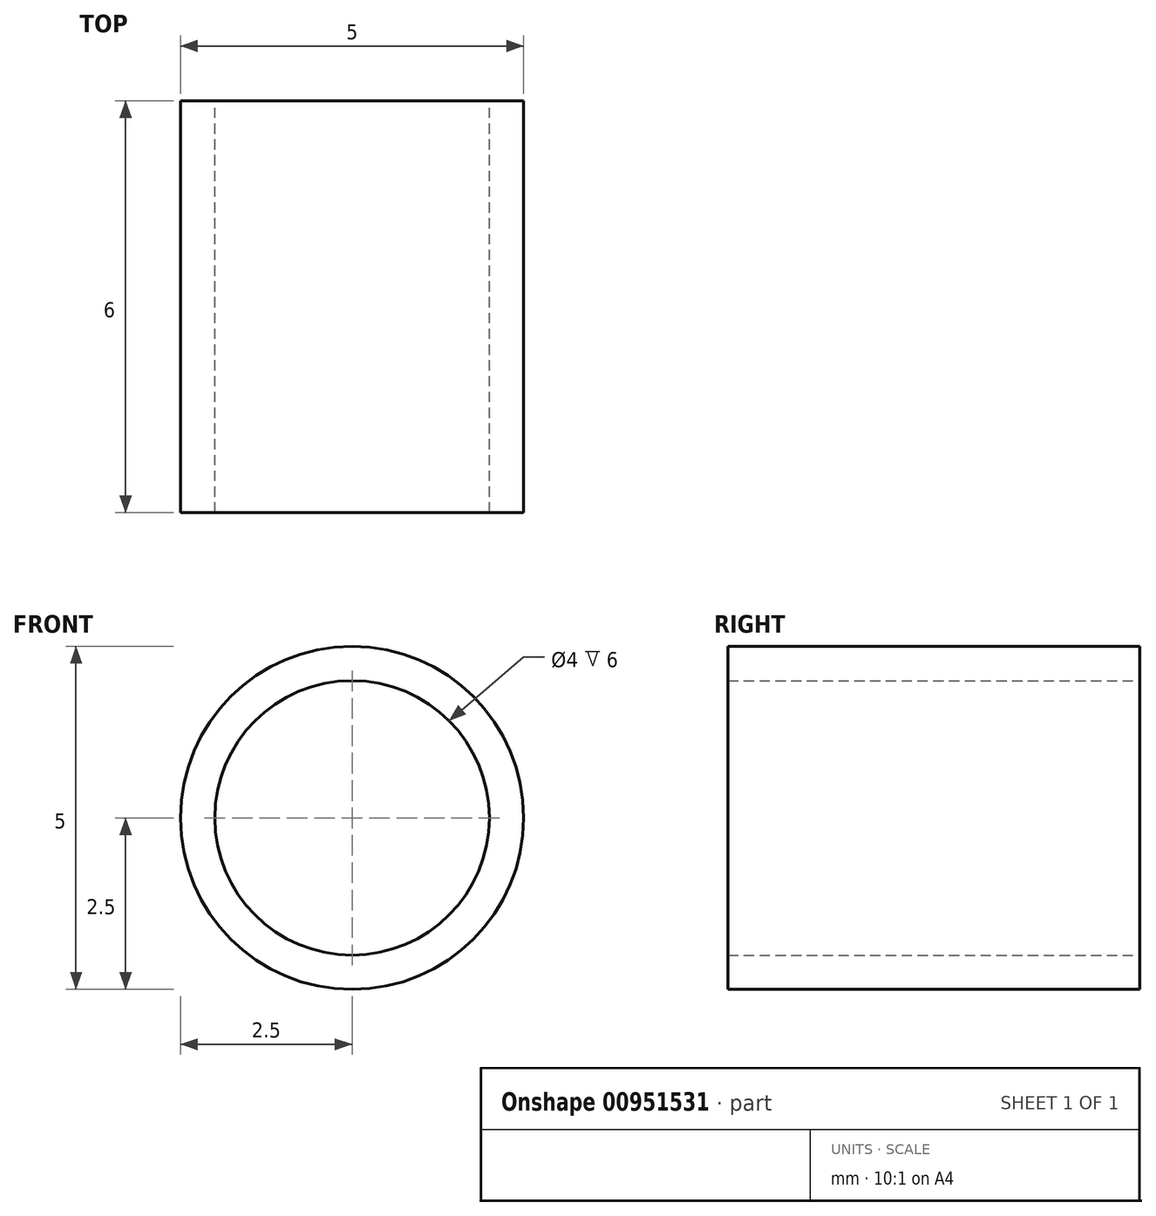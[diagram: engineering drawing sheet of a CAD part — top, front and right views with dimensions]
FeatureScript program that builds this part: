
annotation { "Feature Type Name" : "Feature", "Feature Type Description" : "" }
export const myFeature = defineFeature(function(context is Context, id is Id, definition is map)
    precondition{}
    {
        {
            var Q0;
            Q0=qCreatedBy(makeId("Front.planeOp"),FACE);
            var sketch = newSketch(context, id + "F0", { "sketchPlane" : qUnion([Q0])});
            skCircle(sketch, "E0", {"center": v(0, 0) * mm, "radius": 2.5 * mm});
            skCircle(sketch, "E1", {"center": v(0, 0) * mm, "radius": 2 * mm});
            skSolve(sketch);
        }
        {
            var Q0;
            Q0 = qSketchRegion(id + "F0", true);
            extrude(context, id + "F1", {"entities" : qUnion([Q0]), "depth" : 6 * mm, "offsetDistance" : 25 * mm});
        }
    });
